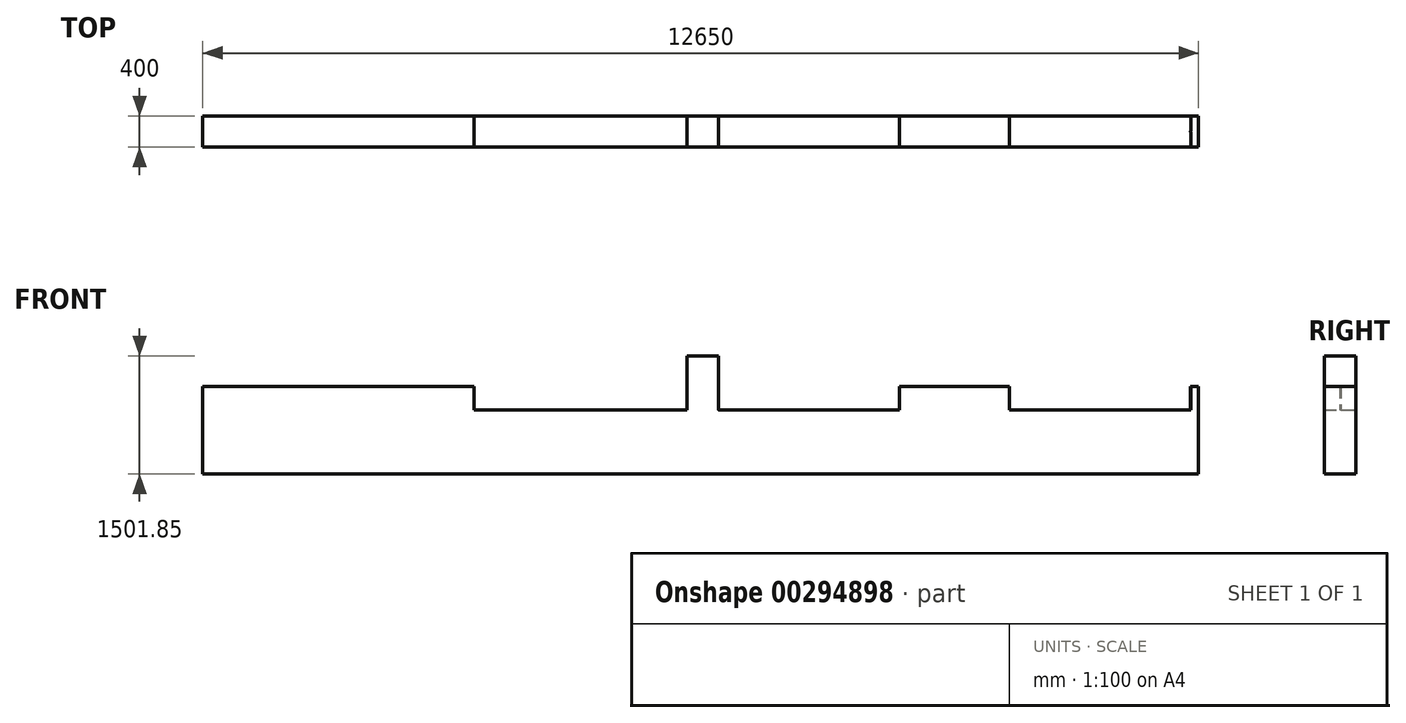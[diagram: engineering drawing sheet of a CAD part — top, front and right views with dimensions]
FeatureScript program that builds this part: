
annotation { "Feature Type Name" : "Feature", "Feature Type Description" : "" }
export const myFeature = defineFeature(function(context is Context, id is Id, definition is map)
    precondition{}
    {
        {
            var Q0;
            Q0=qCreatedBy(makeId("Front.planeOp"),FACE);
            var sketch = newSketch(context, id + "F0", { "sketchPlane" : qUnion([Q0])});
            skLineSegment(sketch, "E0", {"start": v(-6325, 0) * mm, "end": v(6325, 0) * mm});
            skLineSegment(sketch, "E1", {"start": v(-6325, 0) * mm, "end": v(-6325, -812.37) * mm});
            skLineSegment(sketch, "E2", {"start": v(-6325, -812.37) * mm, "end": v(6325, -812.37) * mm});
            skLineSegment(sketch, "E3", {"start": v(6325, -812.37) * mm, "end": v(6325, 0) * mm});
            skLineSegment(sketch, "E4.bottom", {"start": v(-175, 0) * mm, "end": v(225, 0) * mm});
            skLineSegment(sketch, "E4.top", {"start": v(-175, 689.48) * mm, "end": v(225, 689.48) * mm});
            skLineSegment(sketch, "E4.left", {"start": v(-175, 0) * mm, "end": v(-175, 689.48) * mm});
            skLineSegment(sketch, "E4.right", {"start": v(225, 0) * mm, "end": v(225, 689.48) * mm});
            skLineSegment(sketch, "E5.bottom", {"start": v(2525, 0) * mm, "end": v(3925, 0) * mm});
            skLineSegment(sketch, "E5.top", {"start": v(2525, 300) * mm, "end": v(3925, 300) * mm});
            skLineSegment(sketch, "E5.left", {"start": v(2525, 0) * mm, "end": v(2525, 300) * mm});
            skLineSegment(sketch, "E5.right", {"start": v(3925, 0) * mm, "end": v(3925, 300) * mm});
            skLineSegment(sketch, "E6.bottom", {"start": v(6325, 0) * mm, "end": v(6225, 0) * mm});
            skLineSegment(sketch, "E6.top", {"start": v(6325, 300) * mm, "end": v(6225, 300) * mm});
            skLineSegment(sketch, "E6.left", {"start": v(6325, 0) * mm, "end": v(6325, 300) * mm});
            skLineSegment(sketch, "E6.right", {"start": v(6225, 0) * mm, "end": v(6225, 300) * mm});
            skLineSegment(sketch, "E7.bottom", {"start": v(-6325, 0) * mm, "end": v(-2875, 0) * mm});
            skLineSegment(sketch, "E7.top", {"start": v(-6325, 300) * mm, "end": v(-2875, 300) * mm});
            skLineSegment(sketch, "E7.left", {"start": v(-6325, 0) * mm, "end": v(-6325, 300) * mm});
            skLineSegment(sketch, "E7.right", {"start": v(-2875, 0) * mm, "end": v(-2875, 300) * mm});
            skSolve(sketch);
        }
        {
            var Q0;
            Q0=qSketchRegion(id+"F0",true);
            extrude(context, id + "F1", {"entities" : qUnion([Q0]), "depth" : 400 * mm, "offsetDistance" : 25 * mm});
        }
        {
            var Q0;
            {var subQ0=sQuery(id+"F0.wireOp",EDGE,"E0");Q0=makeQuery(id+"F1.opExtrude","SWEPT_FACE",FACE,{"disambiguationData":[OSD([subQ0]),TDD([makeQuery(id+"F0.imprint","IMPRINT",EDGE,{"disambiguationData":[TD([[makeQuery(id+"F0.imprint","INTERSECT",VERTEX,{"derivedFrom":[subQ0,sQuery(id+"F0.wireOp",EDGE,"E4.right")]}),-1.0]])],"derivedFrom":subQ0})])]});}
            var sketch = newSketch(context, id + "F2", { "sketchPlane" : qUnion([Q0])});
            skCircle(sketch, "E8", {"center": v(225, -200) * mm, "radius": 5 * mm});
            skCircle(sketch, "E9", {"center": v(6225, -200) * mm, "radius": 5 * mm});
            skSolve(sketch);
        }
        {
            var Q0;
            Q0=qSketchRegion(id+"F2",true);
            var Q1;
            Q1=makeQuery(id+"F1.opExtrude","SWEPT_FACE",FACE,{"disambiguationData":[OSD([sQuery(id+"F0.wireOp",EDGE,"E6.top")])]});
            extrude(context, id + "F3", {"entities" : qUnion([Q0]), "operationType" : NewBodyOperationType.ADD, "endBound" : BoundingType.UP_TO_SURFACE, "depth" : 25 * mm, "endBoundEntityFace" : qUnion([Q1]), "offsetDistance" : 25 * mm});
        }
    });
